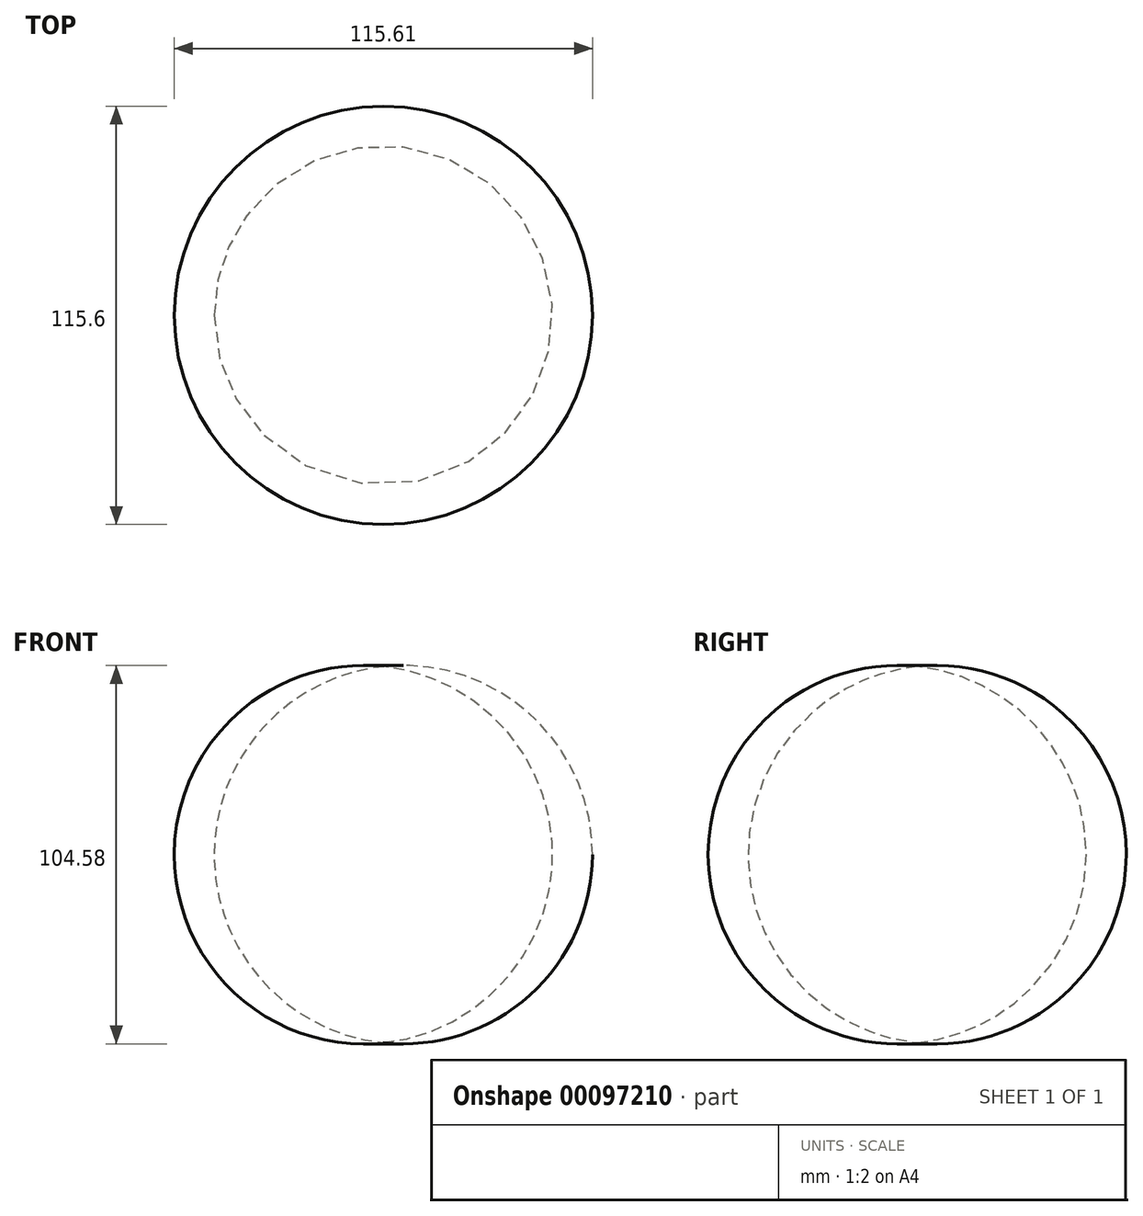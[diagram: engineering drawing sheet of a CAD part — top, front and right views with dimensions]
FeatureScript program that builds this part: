
annotation { "Feature Type Name" : "Feature", "Feature Type Description" : "" }
export const myFeature = defineFeature(function(context is Context, id is Id, definition is map)
    precondition{}
    {
        {
            var Q0;
            Q0=qCreatedBy(makeId("Front.planeOp"),FACE);
            var sketch = newSketch(context, id + "F0", { "sketchPlane" : qUnion([Q0])});
            skLineSegment(sketch, "E0", {"start": v(-47.08, 57.06) * mm, "end": v(-47.08, -46.93) * mm});
            skArc(sketch, "E1", {"start": v(-47.08, -46.93) * mm, "mid": v(-0.3, 5.07) * mm, "end": v(-47.08, 57.06) * mm});
            skSolve(sketch);
        }
        {
            var Q0;
            Q0 = qSketchRegion(id + "F0", true);
            var Q1;
            Q1=makeQuery(id+"F0.imprint","IMPRINT",FACE,{"disambiguationData":[TD([[makeQuery(id+"F0.imprint","IMPRINT",EDGE,{"derivedFrom":sQuery(id+"F0.wireOp",EDGE,"E0")}),1.0]])]});
            var Q2;
            Q2=sQuery(id+"F0.wireOp",EDGE,"E0");
            revolve(context, id + "F1", {"entities" : qUnion([Q0, Q1]), "axis" : qUnion([Q2]), "revolveType" : RevolveType.FULL});
        }
    });
